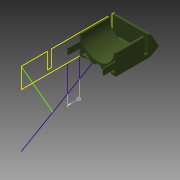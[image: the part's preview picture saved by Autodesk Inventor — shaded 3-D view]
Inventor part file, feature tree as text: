
AUTODESK INVENTOR PART (.ipt)
format: ipt  version: 2013 (Build 170138000, 138)  size: 270,848 bytes
history: native  units: mm
features: sketch x14, extrude x12, other x1, hole x1
ambient origin geometry x8: Origin, YZ Plane, XZ Plane, XY Plane, X Axis, Y Axis, Z Axis, Center Point
feature tree (28):
  other  "ソリッド1"
  extrude  "押し出し1"  Depth=90.0mm
  extrude  "押し出し2"  Depth=50.0mm
  extrude  "押し出し3"  Depth=5.0mm
  extrude  "押し出し4"  Depth=85.0mm
  extrude  "押し出し6"  Depth=5.0mm
  sketch  "スケッチ9"
  hole  "穴1"  [1 undecoded]
  extrude  "押し出し8"  Depth=10.0mm
  extrude  "押し出し9"  Depth=90.0mm
  extrude  "押し出し10"  Depth=230.0mm TaperAngle=0.0deg
  extrude  "押し出し11"  Depth=225.0mm TaperAngle=0.0deg
  extrude  "押し出し12"  Depth=5.0mm TaperAngle=0.0deg
  extrude  "押し出し13"  Depth=65.0mm
  extrude  "押し出し14"  Depth=10.0mm
  sketch  "スケッチ1"
  sketch  "スケッチ2"
  sketch  "スケッチ3"
  sketch  "スケッチ4"
  sketch  "スケッチ6"
  sketch  "スケッチ11"
  sketch  "スケッチ12"
  sketch  "スケッチ13"
  sketch  "スケッチ14"
  sketch  "スケッチ16"
  sketch  "スケッチ17"
  sketch  "スケッチ18"
  sketch  "スケッチ19"
note: 1 required parameter value undecoded (feature->parameter linkage not recoverable at this tier; creation-order binding heuristic only, values carry confidence <= 0.55)
